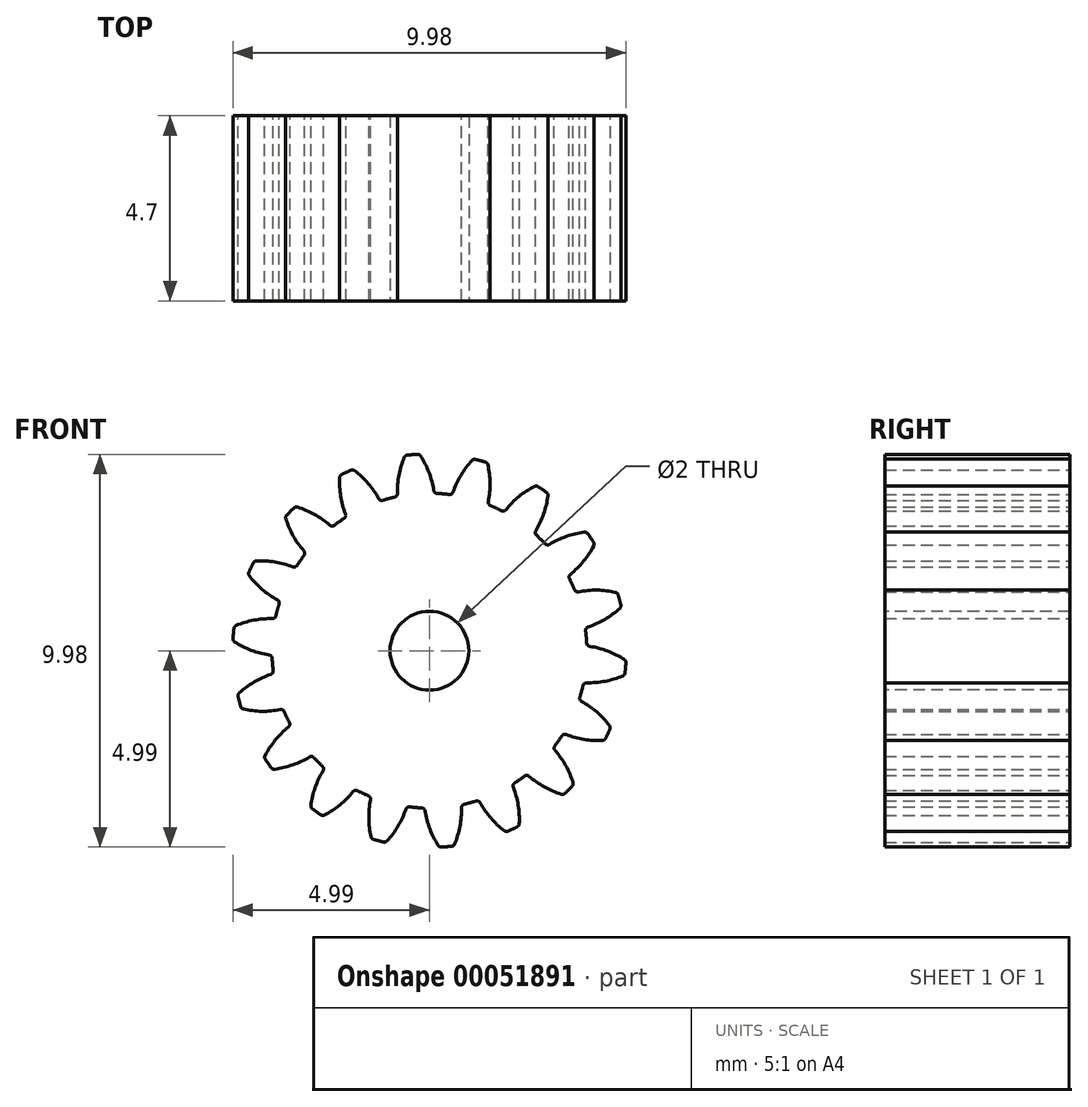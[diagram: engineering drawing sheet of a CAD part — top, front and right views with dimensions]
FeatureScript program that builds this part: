
annotation { "Feature Type Name" : "Feature", "Feature Type Description" : "" }
export const myFeature = defineFeature(function(context is Context, id is Id, definition is map)
    precondition{}
    {
        {
            var Q0;
            Q0=qCreatedBy(makeId("Front.planeOp"),FACE);
            var sketch = newSketch(context, id + "F0", { "sketchPlane" : qUnion([Q0])});
            skCircle(sketch, "E0", {"center": v(0, 0) * mm, "radius": 5 * mm, "construction": true});
            skCircle(sketch, "E1", {"center": v(0, 0) * mm, "radius": 4.5 * mm, "construction": true});
            skCircle(sketch, "E2", {"center": v(0, 0) * mm, "radius": 4 * mm, "construction": true});
            skLineSegment(sketch, "E3", {"start": v(0, 0) * mm, "end": v(0, 8.94) * mm, "construction": true});
            skLineSegment(sketch, "E4", {"start": v(0, 0) * mm, "end": v(-0.76, 8.67) * mm, "construction": true});
            skLineSegment(sketch, "E5", {"start": v(0, 4.5) * mm, "end": v(-8.84, 4.5) * mm, "construction": true});
            skLineSegment(sketch, "E6", {"start": v(0, 4.5) * mm, "end": v(-8.62, 1.36) * mm, "construction": true});
            skCircle(sketch, "E7", {"center": v(0, 4.5) * mm, "radius": 2.25 * mm, "construction": true});
            skCircle(sketch, "E8", {"center": v(-2.11, 3.73) * mm, "radius": 2.25 * mm, "construction": true});
            skArc(sketch, "E9", {"start": v(-0.25, 5) * mm, "mid": v(0, 4.52) * mm, "end": v(0.12, 4) * mm, "construction": true});
            skArc(sketch, "E10", {"start": v(-0.22, 4.95) * mm, "mid": v(-0.01, 4.53) * mm, "end": v(0.1, 4.07) * mm});
            skArc(sketch, "E11.MirrorCS", {"start": v(-0.64, 4.91) * mm, "mid": v(-0.78, 4.46) * mm, "end": v(-0.82, 4) * mm});
            skArc(sketch, "E12", {"start": v(-0.57, 4.97) * mm, "mid": v(-0.44, 4.98) * mm, "end": v(-0.3, 5) * mm});
            skArc(sketch, "E13", {"start": v(-0.89, 3.9) * mm, "mid": v(0.35, -3.98) * mm, "end": v(0.2, 4) * mm});
            skPoint(sketch, "E14.visualSharp", {"position": v(-0.81, 3.92) * mm});
            skArc(sketch, "E14.filletArc", {"start": v(-0.89, 3.9) * mm, "mid": v(-0.83, 3.93) * mm, "end": v(-0.82, 4) * mm});
            skPoint(sketch, "E15.visualSharp", {"position": v(-0.62, 4.96) * mm});
            skArc(sketch, "E15.filletArc", {"start": v(-0.57, 4.97) * mm, "mid": v(-0.61, 4.95) * mm, "end": v(-0.64, 4.91) * mm});
            skPoint(sketch, "E16.visualSharp", {"position": v(0.12, 4) * mm});
            skArc(sketch, "E16.filletArc", {"start": v(0.1, 4.07) * mm, "mid": v(0.14, 4.02) * mm, "end": v(0.2, 4) * mm});
            skPoint(sketch, "E17.visualSharp", {"position": v(-0.25, 5) * mm});
            skArc(sketch, "E17.filletArc", {"start": v(-0.22, 4.95) * mm, "mid": v(-0.26, 4.98) * mm, "end": v(-0.3, 5) * mm});
            skArc(sketch, "E18.1.0", {"start": v(-2.17, 3.36) * mm, "mid": v(-2.13, 3.41) * mm, "end": v(-2.13, 3.47) * mm});
            skArc(sketch, "E18.1.1", {"start": v(-2.28, 4.4) * mm, "mid": v(-2.26, 3.93) * mm, "end": v(-2.13, 3.47) * mm});
            skArc(sketch, "E18.1.2", {"start": v(-2.23, 4.47) * mm, "mid": v(-2.27, 4.44) * mm, "end": v(-2.28, 4.4) * mm});
            skArc(sketch, "E18.1.3", {"start": v(-2.23, 4.47) * mm, "mid": v(-2.11, 4.53) * mm, "end": v(-2, 4.59) * mm});
            skArc(sketch, "E18.1.4", {"start": v(-1.9, 4.57) * mm, "mid": v(-1.95, 4.6) * mm, "end": v(-2, 4.59) * mm});
            skArc(sketch, "E18.1.5", {"start": v(-1.9, 4.57) * mm, "mid": v(-1.56, 4.25) * mm, "end": v(-1.29, 3.86) * mm});
            skArc(sketch, "E18.1.6", {"start": v(-1.29, 3.86) * mm, "mid": v(-1.24, 3.82) * mm, "end": v(-1.18, 3.82) * mm});
            skArc(sketch, "E18.2.0", {"start": v(-3.19, 2.42) * mm, "mid": v(-3.17, 2.48) * mm, "end": v(-3.19, 2.53) * mm});
            skArc(sketch, "E18.2.1", {"start": v(-3.65, 3.35) * mm, "mid": v(-3.46, 2.92) * mm, "end": v(-3.19, 2.53) * mm});
            skArc(sketch, "E18.2.2", {"start": v(-3.63, 3.44) * mm, "mid": v(-3.65, 3.4) * mm, "end": v(-3.65, 3.35) * mm});
            skArc(sketch, "E18.2.3", {"start": v(-3.63, 3.44) * mm, "mid": v(-3.54, 3.54) * mm, "end": v(-3.44, 3.63) * mm});
            skArc(sketch, "E18.2.4", {"start": v(-3.35, 3.65) * mm, "mid": v(-3.4, 3.65) * mm, "end": v(-3.44, 3.63) * mm});
            skArc(sketch, "E18.2.5", {"start": v(-3.35, 3.65) * mm, "mid": v(-2.92, 3.46) * mm, "end": v(-2.53, 3.19) * mm});
            skArc(sketch, "E18.2.6", {"start": v(-2.53, 3.19) * mm, "mid": v(-2.48, 3.17) * mm, "end": v(-2.42, 3.19) * mm});
            skArc(sketch, "E18.3.0", {"start": v(-3.82, 1.18) * mm, "mid": v(-3.82, 1.24) * mm, "end": v(-3.86, 1.29) * mm});
            skArc(sketch, "E18.3.1", {"start": v(-4.57, 1.9) * mm, "mid": v(-4.25, 1.56) * mm, "end": v(-3.86, 1.29) * mm});
            skArc(sketch, "E18.3.2", {"start": v(-4.59, 2) * mm, "mid": v(-4.6, 1.95) * mm, "end": v(-4.57, 1.9) * mm});
            skArc(sketch, "E18.3.3", {"start": v(-4.59, 2) * mm, "mid": v(-4.53, 2.11) * mm, "end": v(-4.47, 2.23) * mm});
            skArc(sketch, "E18.3.4", {"start": v(-4.4, 2.28) * mm, "mid": v(-4.44, 2.27) * mm, "end": v(-4.47, 2.23) * mm});
            skArc(sketch, "E18.3.5", {"start": v(-4.4, 2.28) * mm, "mid": v(-3.93, 2.26) * mm, "end": v(-3.47, 2.13) * mm});
            skArc(sketch, "E18.3.6", {"start": v(-3.47, 2.13) * mm, "mid": v(-3.41, 2.13) * mm, "end": v(-3.36, 2.17) * mm});
            skArc(sketch, "E18.4.0", {"start": v(-4, -0.2) * mm, "mid": v(-4.02, -0.14) * mm, "end": v(-4.07, -0.1) * mm});
            skArc(sketch, "E18.4.1", {"start": v(-4.95, 0.22) * mm, "mid": v(-4.53, 0.01) * mm, "end": v(-4.07, -0.1) * mm});
            skArc(sketch, "E18.4.2", {"start": v(-5, 0.3) * mm, "mid": v(-4.98, 0.26) * mm, "end": v(-4.95, 0.22) * mm});
            skArc(sketch, "E18.4.3", {"start": v(-5, 0.3) * mm, "mid": v(-4.98, 0.44) * mm, "end": v(-4.97, 0.57) * mm});
            skArc(sketch, "E18.4.4", {"start": v(-4.91, 0.64) * mm, "mid": v(-4.95, 0.61) * mm, "end": v(-4.97, 0.57) * mm});
            skArc(sketch, "E18.4.5", {"start": v(-4.91, 0.64) * mm, "mid": v(-4.46, 0.78) * mm, "end": v(-4, 0.82) * mm});
            skArc(sketch, "E18.4.6", {"start": v(-4, 0.82) * mm, "mid": v(-3.93, 0.83) * mm, "end": v(-3.9, 0.89) * mm});
            skArc(sketch, "E18.5.0", {"start": v(-3.69, -1.55) * mm, "mid": v(-3.73, -1.5) * mm, "end": v(-3.79, -1.5) * mm});
            skArc(sketch, "E18.5.1", {"start": v(-4.73, -1.48) * mm, "mid": v(-4.26, -1.54) * mm, "end": v(-3.79, -1.5) * mm});
            skArc(sketch, "E18.5.2", {"start": v(-4.8, -1.42) * mm, "mid": v(-4.77, -1.46) * mm, "end": v(-4.73, -1.48) * mm});
            skArc(sketch, "E18.5.3", {"start": v(-4.8, -1.42) * mm, "mid": v(-4.83, -1.3) * mm, "end": v(-4.86, -1.17) * mm});
            skArc(sketch, "E18.5.4", {"start": v(-4.84, -1.08) * mm, "mid": v(-4.86, -1.12) * mm, "end": v(-4.86, -1.17) * mm});
            skArc(sketch, "E18.5.5", {"start": v(-4.84, -1.08) * mm, "mid": v(-4.46, -0.8) * mm, "end": v(-4.03, -0.6) * mm});
            skArc(sketch, "E18.5.6", {"start": v(-4.03, -0.6) * mm, "mid": v(-3.98, -0.56) * mm, "end": v(-3.97, -0.5) * mm});
            skArc(sketch, "E18.6.0", {"start": v(-2.94, -2.72) * mm, "mid": v(-2.99, -2.69) * mm, "end": v(-3.05, -2.7) * mm});
            skArc(sketch, "E18.6.1", {"start": v(-3.94, -3.01) * mm, "mid": v(-3.48, -2.9) * mm, "end": v(-3.05, -2.7) * mm});
            skArc(sketch, "E18.6.2", {"start": v(-4.02, -2.97) * mm, "mid": v(-3.98, -3) * mm, "end": v(-3.94, -3.01) * mm});
            skArc(sketch, "E18.6.3", {"start": v(-4.02, -2.97) * mm, "mid": v(-4.1, -2.87) * mm, "end": v(-4.17, -2.76) * mm});
            skArc(sketch, "E18.6.4", {"start": v(-4.17, -2.67) * mm, "mid": v(-4.18, -2.71) * mm, "end": v(-4.17, -2.76) * mm});
            skArc(sketch, "E18.6.5", {"start": v(-4.17, -2.67) * mm, "mid": v(-3.92, -2.27) * mm, "end": v(-3.58, -1.94) * mm});
            skArc(sketch, "E18.6.6", {"start": v(-3.58, -1.94) * mm, "mid": v(-3.55, -1.89) * mm, "end": v(-3.56, -1.83) * mm});
            skArc(sketch, "E18.7.0", {"start": v(-1.83, -3.56) * mm, "mid": v(-1.89, -3.55) * mm, "end": v(-1.94, -3.58) * mm});
            skArc(sketch, "E18.7.1", {"start": v(-2.67, -4.17) * mm, "mid": v(-2.27, -3.92) * mm, "end": v(-1.94, -3.58) * mm});
            skArc(sketch, "E18.7.2", {"start": v(-2.76, -4.17) * mm, "mid": v(-2.71, -4.18) * mm, "end": v(-2.67, -4.17) * mm});
            skArc(sketch, "E18.7.3", {"start": v(-2.76, -4.17) * mm, "mid": v(-2.87, -4.1) * mm, "end": v(-2.97, -4.02) * mm});
            skArc(sketch, "E18.7.4", {"start": v(-3.01, -3.94) * mm, "mid": v(-3, -3.98) * mm, "end": v(-2.97, -4.02) * mm});
            skArc(sketch, "E18.7.5", {"start": v(-3.01, -3.94) * mm, "mid": v(-2.9, -3.48) * mm, "end": v(-2.7, -3.05) * mm});
            skArc(sketch, "E18.7.6", {"start": v(-2.7, -3.05) * mm, "mid": v(-2.69, -2.99) * mm, "end": v(-2.72, -2.94) * mm});
            skArc(sketch, "E18.8.0", {"start": v(-0.5, -3.97) * mm, "mid": v(-0.56, -3.98) * mm, "end": v(-0.6, -4.03) * mm});
            skArc(sketch, "E18.8.1", {"start": v(-1.08, -4.84) * mm, "mid": v(-0.8, -4.46) * mm, "end": v(-0.6, -4.03) * mm});
            skArc(sketch, "E18.8.2", {"start": v(-1.17, -4.86) * mm, "mid": v(-1.12, -4.86) * mm, "end": v(-1.08, -4.84) * mm});
            skArc(sketch, "E18.8.3", {"start": v(-1.17, -4.86) * mm, "mid": v(-1.3, -4.83) * mm, "end": v(-1.42, -4.8) * mm});
            skArc(sketch, "E18.8.4", {"start": v(-1.48, -4.73) * mm, "mid": v(-1.46, -4.77) * mm, "end": v(-1.42, -4.8) * mm});
            skArc(sketch, "E18.8.5", {"start": v(-1.48, -4.73) * mm, "mid": v(-1.54, -4.26) * mm, "end": v(-1.5, -3.79) * mm});
            skArc(sketch, "E18.8.6", {"start": v(-1.5, -3.79) * mm, "mid": v(-1.5, -3.73) * mm, "end": v(-1.55, -3.69) * mm});
            skArc(sketch, "E18.9.0", {"start": v(0.89, -3.9) * mm, "mid": v(0.83, -3.93) * mm, "end": v(0.82, -4) * mm});
            skArc(sketch, "E18.9.1", {"start": v(0.64, -4.91) * mm, "mid": v(0.78, -4.46) * mm, "end": v(0.82, -4) * mm});
            skArc(sketch, "E18.9.2", {"start": v(0.57, -4.97) * mm, "mid": v(0.61, -4.95) * mm, "end": v(0.64, -4.91) * mm});
            skArc(sketch, "E18.9.3", {"start": v(0.57, -4.97) * mm, "mid": v(0.44, -4.98) * mm, "end": v(0.3, -5) * mm});
            skArc(sketch, "E18.9.4", {"start": v(0.22, -4.95) * mm, "mid": v(0.26, -4.98) * mm, "end": v(0.3, -5) * mm});
            skArc(sketch, "E18.9.5", {"start": v(0.22, -4.95) * mm, "mid": v(0.01, -4.53) * mm, "end": v(-0.1, -4.07) * mm});
            skArc(sketch, "E18.9.6", {"start": v(-0.1, -4.07) * mm, "mid": v(-0.14, -4.02) * mm, "end": v(-0.2, -4) * mm});
            skArc(sketch, "E18.10.0", {"start": v(2.17, -3.36) * mm, "mid": v(2.13, -3.41) * mm, "end": v(2.13, -3.47) * mm});
            skArc(sketch, "E18.10.1", {"start": v(2.28, -4.4) * mm, "mid": v(2.26, -3.93) * mm, "end": v(2.13, -3.47) * mm});
            skArc(sketch, "E18.10.2", {"start": v(2.23, -4.47) * mm, "mid": v(2.27, -4.44) * mm, "end": v(2.28, -4.4) * mm});
            skArc(sketch, "E18.10.3", {"start": v(2.23, -4.47) * mm, "mid": v(2.11, -4.53) * mm, "end": v(2, -4.59) * mm});
            skArc(sketch, "E18.10.4", {"start": v(1.9, -4.57) * mm, "mid": v(1.95, -4.6) * mm, "end": v(2, -4.59) * mm});
            skArc(sketch, "E18.10.5", {"start": v(1.9, -4.57) * mm, "mid": v(1.56, -4.25) * mm, "end": v(1.29, -3.86) * mm});
            skArc(sketch, "E18.10.6", {"start": v(1.29, -3.86) * mm, "mid": v(1.24, -3.82) * mm, "end": v(1.18, -3.82) * mm});
            skArc(sketch, "E18.11.0", {"start": v(3.19, -2.42) * mm, "mid": v(3.17, -2.48) * mm, "end": v(3.19, -2.53) * mm});
            skArc(sketch, "E18.11.1", {"start": v(3.65, -3.35) * mm, "mid": v(3.46, -2.92) * mm, "end": v(3.19, -2.53) * mm});
            skArc(sketch, "E18.11.2", {"start": v(3.63, -3.44) * mm, "mid": v(3.65, -3.4) * mm, "end": v(3.65, -3.35) * mm});
            skArc(sketch, "E18.11.3", {"start": v(3.63, -3.44) * mm, "mid": v(3.54, -3.54) * mm, "end": v(3.44, -3.63) * mm});
            skArc(sketch, "E18.11.4", {"start": v(3.35, -3.65) * mm, "mid": v(3.4, -3.65) * mm, "end": v(3.44, -3.63) * mm});
            skArc(sketch, "E18.11.5", {"start": v(3.35, -3.65) * mm, "mid": v(2.92, -3.46) * mm, "end": v(2.53, -3.19) * mm});
            skArc(sketch, "E18.11.6", {"start": v(2.53, -3.19) * mm, "mid": v(2.48, -3.17) * mm, "end": v(2.42, -3.19) * mm});
            skArc(sketch, "E18.12.0", {"start": v(3.82, -1.18) * mm, "mid": v(3.82, -1.24) * mm, "end": v(3.86, -1.29) * mm});
            skArc(sketch, "E18.12.1", {"start": v(4.57, -1.9) * mm, "mid": v(4.25, -1.56) * mm, "end": v(3.86, -1.29) * mm});
            skArc(sketch, "E18.12.2", {"start": v(4.59, -2) * mm, "mid": v(4.6, -1.95) * mm, "end": v(4.57, -1.9) * mm});
            skArc(sketch, "E18.12.3", {"start": v(4.59, -2) * mm, "mid": v(4.53, -2.11) * mm, "end": v(4.47, -2.23) * mm});
            skArc(sketch, "E18.12.4", {"start": v(4.4, -2.28) * mm, "mid": v(4.44, -2.27) * mm, "end": v(4.47, -2.23) * mm});
            skArc(sketch, "E18.12.5", {"start": v(4.4, -2.28) * mm, "mid": v(3.93, -2.26) * mm, "end": v(3.47, -2.13) * mm});
            skArc(sketch, "E18.12.6", {"start": v(3.47, -2.13) * mm, "mid": v(3.41, -2.13) * mm, "end": v(3.36, -2.17) * mm});
            skArc(sketch, "E18.13.0", {"start": v(4, 0.2) * mm, "mid": v(4.02, 0.14) * mm, "end": v(4.07, 0.1) * mm});
            skArc(sketch, "E18.13.1", {"start": v(4.95, -0.22) * mm, "mid": v(4.53, -0.01) * mm, "end": v(4.07, 0.1) * mm});
            skArc(sketch, "E18.13.2", {"start": v(5, -0.3) * mm, "mid": v(4.98, -0.26) * mm, "end": v(4.95, -0.22) * mm});
            skArc(sketch, "E18.13.3", {"start": v(5, -0.3) * mm, "mid": v(4.98, -0.44) * mm, "end": v(4.97, -0.57) * mm});
            skArc(sketch, "E18.13.4", {"start": v(4.91, -0.64) * mm, "mid": v(4.95, -0.61) * mm, "end": v(4.97, -0.57) * mm});
            skArc(sketch, "E18.13.5", {"start": v(4.91, -0.64) * mm, "mid": v(4.46, -0.78) * mm, "end": v(4, -0.82) * mm});
            skArc(sketch, "E18.13.6", {"start": v(4, -0.82) * mm, "mid": v(3.93, -0.83) * mm, "end": v(3.9, -0.89) * mm});
            skArc(sketch, "E18.14.0", {"start": v(3.69, 1.55) * mm, "mid": v(3.73, 1.5) * mm, "end": v(3.79, 1.5) * mm});
            skArc(sketch, "E18.14.1", {"start": v(4.73, 1.48) * mm, "mid": v(4.26, 1.54) * mm, "end": v(3.79, 1.5) * mm});
            skArc(sketch, "E18.14.2", {"start": v(4.8, 1.42) * mm, "mid": v(4.77, 1.46) * mm, "end": v(4.73, 1.48) * mm});
            skArc(sketch, "E18.14.3", {"start": v(4.8, 1.42) * mm, "mid": v(4.83, 1.3) * mm, "end": v(4.86, 1.17) * mm});
            skArc(sketch, "E18.14.4", {"start": v(4.84, 1.08) * mm, "mid": v(4.86, 1.12) * mm, "end": v(4.86, 1.17) * mm});
            skArc(sketch, "E18.14.5", {"start": v(4.84, 1.08) * mm, "mid": v(4.46, 0.8) * mm, "end": v(4.03, 0.6) * mm});
            skArc(sketch, "E18.14.6", {"start": v(4.03, 0.6) * mm, "mid": v(3.98, 0.56) * mm, "end": v(3.97, 0.5) * mm});
            skArc(sketch, "E18.15.0", {"start": v(2.94, 2.72) * mm, "mid": v(2.99, 2.69) * mm, "end": v(3.05, 2.7) * mm});
            skArc(sketch, "E18.15.1", {"start": v(3.94, 3.01) * mm, "mid": v(3.48, 2.9) * mm, "end": v(3.05, 2.7) * mm});
            skArc(sketch, "E18.15.2", {"start": v(4.02, 2.97) * mm, "mid": v(3.98, 3) * mm, "end": v(3.94, 3.01) * mm});
            skArc(sketch, "E18.15.3", {"start": v(4.02, 2.97) * mm, "mid": v(4.1, 2.87) * mm, "end": v(4.17, 2.76) * mm});
            skArc(sketch, "E18.15.4", {"start": v(4.17, 2.67) * mm, "mid": v(4.18, 2.71) * mm, "end": v(4.17, 2.76) * mm});
            skArc(sketch, "E18.15.5", {"start": v(4.17, 2.67) * mm, "mid": v(3.92, 2.27) * mm, "end": v(3.58, 1.94) * mm});
            skArc(sketch, "E18.15.6", {"start": v(3.58, 1.94) * mm, "mid": v(3.55, 1.89) * mm, "end": v(3.56, 1.83) * mm});
            skArc(sketch, "E18.16.0", {"start": v(1.83, 3.56) * mm, "mid": v(1.89, 3.55) * mm, "end": v(1.94, 3.58) * mm});
            skArc(sketch, "E18.16.1", {"start": v(2.67, 4.17) * mm, "mid": v(2.27, 3.92) * mm, "end": v(1.94, 3.58) * mm});
            skArc(sketch, "E18.16.2", {"start": v(2.76, 4.17) * mm, "mid": v(2.71, 4.18) * mm, "end": v(2.67, 4.17) * mm});
            skArc(sketch, "E18.16.3", {"start": v(2.76, 4.17) * mm, "mid": v(2.87, 4.1) * mm, "end": v(2.97, 4.02) * mm});
            skArc(sketch, "E18.16.4", {"start": v(3.01, 3.94) * mm, "mid": v(3, 3.98) * mm, "end": v(2.97, 4.02) * mm});
            skArc(sketch, "E18.16.5", {"start": v(3.01, 3.94) * mm, "mid": v(2.9, 3.48) * mm, "end": v(2.7, 3.05) * mm});
            skArc(sketch, "E18.16.6", {"start": v(2.7, 3.05) * mm, "mid": v(2.69, 2.99) * mm, "end": v(2.72, 2.94) * mm});
            skArc(sketch, "E18.17.0", {"start": v(0.5, 3.97) * mm, "mid": v(0.56, 3.98) * mm, "end": v(0.6, 4.03) * mm});
            skArc(sketch, "E18.17.1", {"start": v(1.08, 4.84) * mm, "mid": v(0.8, 4.46) * mm, "end": v(0.6, 4.03) * mm});
            skArc(sketch, "E18.17.2", {"start": v(1.17, 4.86) * mm, "mid": v(1.12, 4.86) * mm, "end": v(1.08, 4.84) * mm});
            skArc(sketch, "E18.17.3", {"start": v(1.17, 4.86) * mm, "mid": v(1.3, 4.83) * mm, "end": v(1.42, 4.8) * mm});
            skArc(sketch, "E18.17.4", {"start": v(1.48, 4.73) * mm, "mid": v(1.46, 4.77) * mm, "end": v(1.42, 4.8) * mm});
            skArc(sketch, "E18.17.5", {"start": v(1.48, 4.73) * mm, "mid": v(1.54, 4.26) * mm, "end": v(1.5, 3.79) * mm});
            skArc(sketch, "E18.17.6", {"start": v(1.5, 3.79) * mm, "mid": v(1.5, 3.73) * mm, "end": v(1.55, 3.69) * mm});
            skSolve(sketch);
        }
        {
            var Q0;
            Q0 = qSketchRegion(id + "F0", true);
            var Q1;
            Q1=makeQuery(id+"F0.imprint","IMPRINT",FACE,{"disambiguationData":[TD([[makeQuery(id+"F0.imprint","IMPRINT",EDGE,{"derivedFrom":sQuery(id+"F0.wireOp",EDGE,"E10")}),-1.0]])]});
            extrude(context, id + "F1", {"entities" : qUnion([Q0, Q1]), "depth" : 4.7 * mm});
        }
        {
            var Q0;
            Q0=makeQuery(id+"F1.opExtrude","CAP_FACE",FACE,{"disambiguationData":[OSD([sQuery(id+"F0.wireOp",EDGE,"E10"),sQuery(id+"F0.wireOp",EDGE,"E11.MirrorCS"),sQuery(id+"F0.wireOp",EDGE,"E12"),sQuery(id+"F0.wireOp",EDGE,"E13"),sQuery(id+"F0.wireOp",EDGE,"E14.filletArc"),sQuery(id+"F0.wireOp",EDGE,"E15.filletArc"),sQuery(id+"F0.wireOp",EDGE,"E16.filletArc"),sQuery(id+"F0.wireOp",EDGE,"E17.filletArc"),sQuery(id+"F0.wireOp",EDGE,"E18.1.0"),sQuery(id+"F0.wireOp",EDGE,"E18.1.1"),sQuery(id+"F0.wireOp",EDGE,"E18.1.2"),sQuery(id+"F0.wireOp",EDGE,"E18.1.3"),sQuery(id+"F0.wireOp",EDGE,"E18.1.4"),sQuery(id+"F0.wireOp",EDGE,"E18.1.5"),sQuery(id+"F0.wireOp",EDGE,"E18.1.6"),sQuery(id+"F0.wireOp",EDGE,"E18.2.0"),sQuery(id+"F0.wireOp",EDGE,"E18.2.1"),sQuery(id+"F0.wireOp",EDGE,"E18.2.2"),sQuery(id+"F0.wireOp",EDGE,"E18.2.3"),sQuery(id+"F0.wireOp",EDGE,"E18.2.4"),sQuery(id+"F0.wireOp",EDGE,"E18.2.5"),sQuery(id+"F0.wireOp",EDGE,"E18.2.6"),sQuery(id+"F0.wireOp",EDGE,"E18.3.0"),sQuery(id+"F0.wireOp",EDGE,"E18.3.1"),sQuery(id+"F0.wireOp",EDGE,"E18.3.2"),sQuery(id+"F0.wireOp",EDGE,"E18.3.3"),sQuery(id+"F0.wireOp",EDGE,"E18.3.4"),sQuery(id+"F0.wireOp",EDGE,"E18.3.5"),sQuery(id+"F0.wireOp",EDGE,"E18.3.6"),sQuery(id+"F0.wireOp",EDGE,"E18.4.0"),sQuery(id+"F0.wireOp",EDGE,"E18.4.1"),sQuery(id+"F0.wireOp",EDGE,"E18.4.2"),sQuery(id+"F0.wireOp",EDGE,"E18.4.3"),sQuery(id+"F0.wireOp",EDGE,"E18.4.4"),sQuery(id+"F0.wireOp",EDGE,"E18.4.5"),sQuery(id+"F0.wireOp",EDGE,"E18.4.6"),sQuery(id+"F0.wireOp",EDGE,"E18.5.0"),sQuery(id+"F0.wireOp",EDGE,"E18.5.1"),sQuery(id+"F0.wireOp",EDGE,"E18.5.2"),sQuery(id+"F0.wireOp",EDGE,"E18.5.3"),sQuery(id+"F0.wireOp",EDGE,"E18.5.4"),sQuery(id+"F0.wireOp",EDGE,"E18.5.5"),sQuery(id+"F0.wireOp",EDGE,"E18.5.6"),sQuery(id+"F0.wireOp",EDGE,"E18.6.0"),sQuery(id+"F0.wireOp",EDGE,"E18.6.1"),sQuery(id+"F0.wireOp",EDGE,"E18.6.2"),sQuery(id+"F0.wireOp",EDGE,"E18.6.3"),sQuery(id+"F0.wireOp",EDGE,"E18.6.4"),sQuery(id+"F0.wireOp",EDGE,"E18.6.5"),sQuery(id+"F0.wireOp",EDGE,"E18.6.6"),sQuery(id+"F0.wireOp",EDGE,"E18.7.0"),sQuery(id+"F0.wireOp",EDGE,"E18.7.1"),sQuery(id+"F0.wireOp",EDGE,"E18.7.2"),sQuery(id+"F0.wireOp",EDGE,"E18.7.3"),sQuery(id+"F0.wireOp",EDGE,"E18.7.4"),sQuery(id+"F0.wireOp",EDGE,"E18.7.5"),sQuery(id+"F0.wireOp",EDGE,"E18.7.6"),sQuery(id+"F0.wireOp",EDGE,"E18.8.0"),sQuery(id+"F0.wireOp",EDGE,"E18.8.1"),sQuery(id+"F0.wireOp",EDGE,"E18.8.2"),sQuery(id+"F0.wireOp",EDGE,"E18.8.3"),sQuery(id+"F0.wireOp",EDGE,"E18.8.4"),sQuery(id+"F0.wireOp",EDGE,"E18.8.5"),sQuery(id+"F0.wireOp",EDGE,"E18.8.6"),sQuery(id+"F0.wireOp",EDGE,"E18.9.0"),sQuery(id+"F0.wireOp",EDGE,"E18.9.1"),sQuery(id+"F0.wireOp",EDGE,"E18.9.2"),sQuery(id+"F0.wireOp",EDGE,"E18.9.3"),sQuery(id+"F0.wireOp",EDGE,"E18.9.4"),sQuery(id+"F0.wireOp",EDGE,"E18.9.5"),sQuery(id+"F0.wireOp",EDGE,"E18.9.6"),sQuery(id+"F0.wireOp",EDGE,"E18.10.0"),sQuery(id+"F0.wireOp",EDGE,"E18.10.1"),sQuery(id+"F0.wireOp",EDGE,"E18.10.2"),sQuery(id+"F0.wireOp",EDGE,"E18.10.3"),sQuery(id+"F0.wireOp",EDGE,"E18.10.4"),sQuery(id+"F0.wireOp",EDGE,"E18.10.5"),sQuery(id+"F0.wireOp",EDGE,"E18.10.6"),sQuery(id+"F0.wireOp",EDGE,"E18.11.0"),sQuery(id+"F0.wireOp",EDGE,"E18.11.1"),sQuery(id+"F0.wireOp",EDGE,"E18.11.2"),sQuery(id+"F0.wireOp",EDGE,"E18.11.3"),sQuery(id+"F0.wireOp",EDGE,"E18.11.4"),sQuery(id+"F0.wireOp",EDGE,"E18.11.5"),sQuery(id+"F0.wireOp",EDGE,"E18.11.6"),sQuery(id+"F0.wireOp",EDGE,"E18.12.0"),sQuery(id+"F0.wireOp",EDGE,"E18.12.1"),sQuery(id+"F0.wireOp",EDGE,"E18.12.2"),sQuery(id+"F0.wireOp",EDGE,"E18.12.3"),sQuery(id+"F0.wireOp",EDGE,"E18.12.4"),sQuery(id+"F0.wireOp",EDGE,"E18.12.5"),sQuery(id+"F0.wireOp",EDGE,"E18.12.6"),sQuery(id+"F0.wireOp",EDGE,"E18.13.0"),sQuery(id+"F0.wireOp",EDGE,"E18.13.1"),sQuery(id+"F0.wireOp",EDGE,"E18.13.2"),sQuery(id+"F0.wireOp",EDGE,"E18.13.3"),sQuery(id+"F0.wireOp",EDGE,"E18.13.4"),sQuery(id+"F0.wireOp",EDGE,"E18.13.5"),sQuery(id+"F0.wireOp",EDGE,"E18.13.6"),sQuery(id+"F0.wireOp",EDGE,"E18.14.0"),sQuery(id+"F0.wireOp",EDGE,"E18.14.1"),sQuery(id+"F0.wireOp",EDGE,"E18.14.2"),sQuery(id+"F0.wireOp",EDGE,"E18.14.3"),sQuery(id+"F0.wireOp",EDGE,"E18.14.4"),sQuery(id+"F0.wireOp",EDGE,"E18.14.5"),sQuery(id+"F0.wireOp",EDGE,"E18.14.6"),sQuery(id+"F0.wireOp",EDGE,"E18.15.0"),sQuery(id+"F0.wireOp",EDGE,"E18.15.1"),sQuery(id+"F0.wireOp",EDGE,"E18.15.2"),sQuery(id+"F0.wireOp",EDGE,"E18.15.3"),sQuery(id+"F0.wireOp",EDGE,"E18.15.4"),sQuery(id+"F0.wireOp",EDGE,"E18.15.5"),sQuery(id+"F0.wireOp",EDGE,"E18.15.6"),sQuery(id+"F0.wireOp",EDGE,"E18.16.0"),sQuery(id+"F0.wireOp",EDGE,"E18.16.1"),sQuery(id+"F0.wireOp",EDGE,"E18.16.2"),sQuery(id+"F0.wireOp",EDGE,"E18.16.3"),sQuery(id+"F0.wireOp",EDGE,"E18.16.4"),sQuery(id+"F0.wireOp",EDGE,"E18.16.5"),sQuery(id+"F0.wireOp",EDGE,"E18.16.6"),sQuery(id+"F0.wireOp",EDGE,"E18.17.0"),sQuery(id+"F0.wireOp",EDGE,"E18.17.1"),sQuery(id+"F0.wireOp",EDGE,"E18.17.2"),sQuery(id+"F0.wireOp",EDGE,"E18.17.3"),sQuery(id+"F0.wireOp",EDGE,"E18.17.4"),sQuery(id+"F0.wireOp",EDGE,"E18.17.5"),sQuery(id+"F0.wireOp",EDGE,"E18.17.6")])],"isStart":false});
            var sketch = newSketch(context, id + "F2", { "sketchPlane" : qUnion([Q0])});
            skCircle(sketch, "E19", {"center": v(0, 0) * mm, "radius": 1 * mm});
            skSolve(sketch);
        }
        {
            var Q0;
            Q0 = qSketchRegion(id + "F2", true);
            extrude(context, id + "F3", {"entities" : qUnion([Q0]), "operationType" : NewBodyOperationType.REMOVE, "endBound" : BoundingType.THROUGH_ALL, "oppositeDirection" : true, "depth" : 25 * mm});
        }
    });
